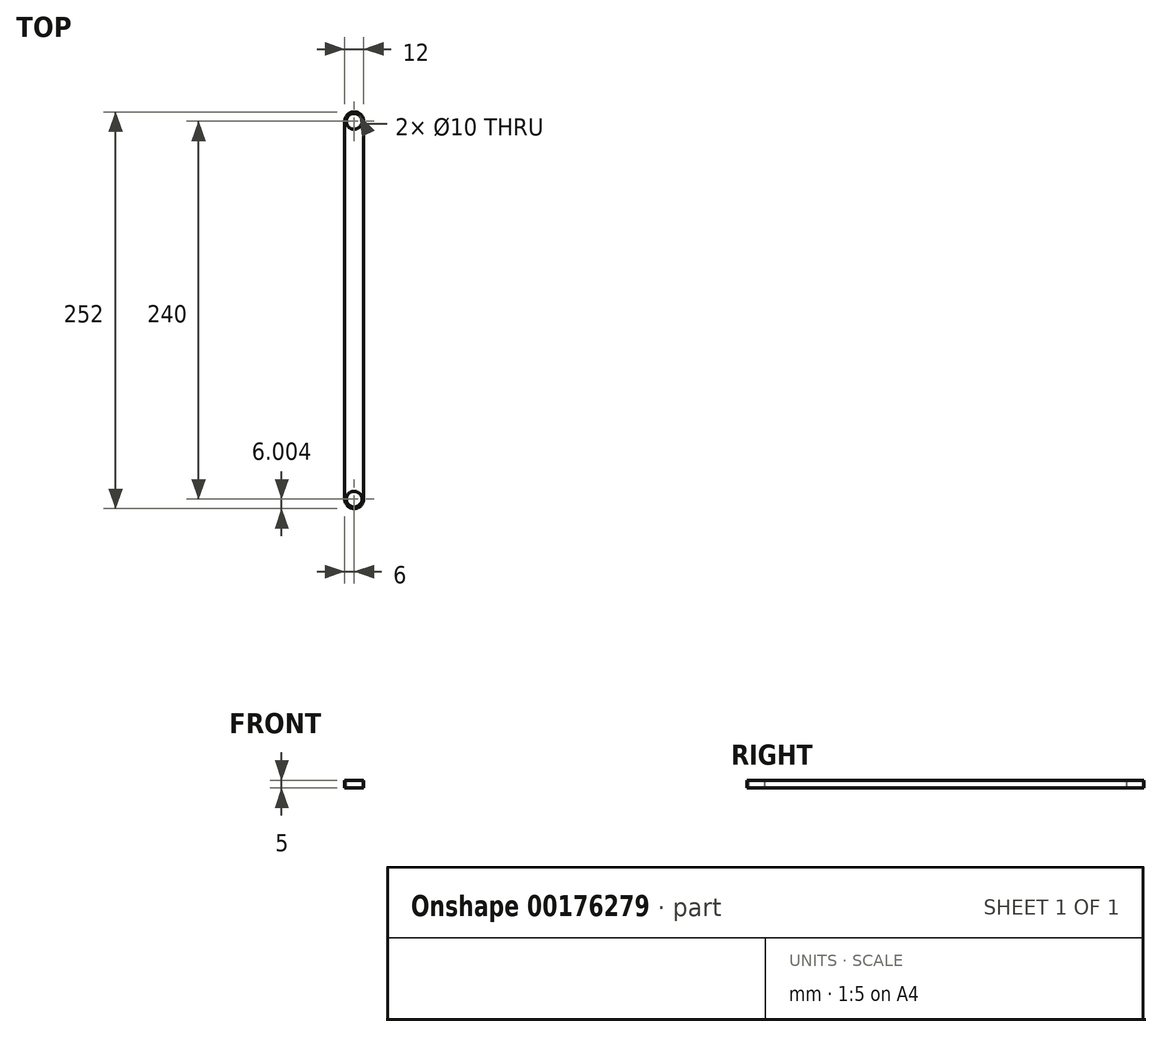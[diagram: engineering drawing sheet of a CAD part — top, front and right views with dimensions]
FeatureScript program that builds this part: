
annotation { "Feature Type Name" : "Feature", "Feature Type Description" : "" }
export const myFeature = defineFeature(function(context is Context, id is Id, definition is map)
    precondition{}
    {
        {
            var Q0;
            Q0=qCreatedBy(makeId("Top.planeOp"),FACE);
            var sketch = newSketch(context, id + "F0", { "sketchPlane" : qUnion([Q0])});
            skLineSegment(sketch, "E0.left", {"start": v(-77.99, 153.17) * mm, "end": v(-77.99, -86.83) * mm});
            skLineSegment(sketch, "E0.right", {"start": v(-65.99, 153.17) * mm, "end": v(-65.99, -86.83) * mm});
            skArc(sketch, "E1", {"start": v(-65.99, 153.17) * mm, "mid": v(-71.99, 159.17) * mm, "end": v(-77.99, 153.17) * mm});
            skCircle(sketch, "E2", {"center": v(-71.99, 153.17) * mm, "radius": 5 * mm});
            skArc(sketch, "E3", {"start": v(-77.99, -86.83) * mm, "mid": v(-71.99, -92.83) * mm, "end": v(-65.99, -86.83) * mm});
            skCircle(sketch, "E4", {"center": v(-71.99, -86.83) * mm, "radius": 5 * mm});
            skSolve(sketch);
        }
        {
            var Q0;
            Q0 = qSketchRegion(id + "F0", true);
            extrude(context, id + "F1", {"entities" : qUnion([Q0]), "depth" : 5 * mm});
        }
    });
